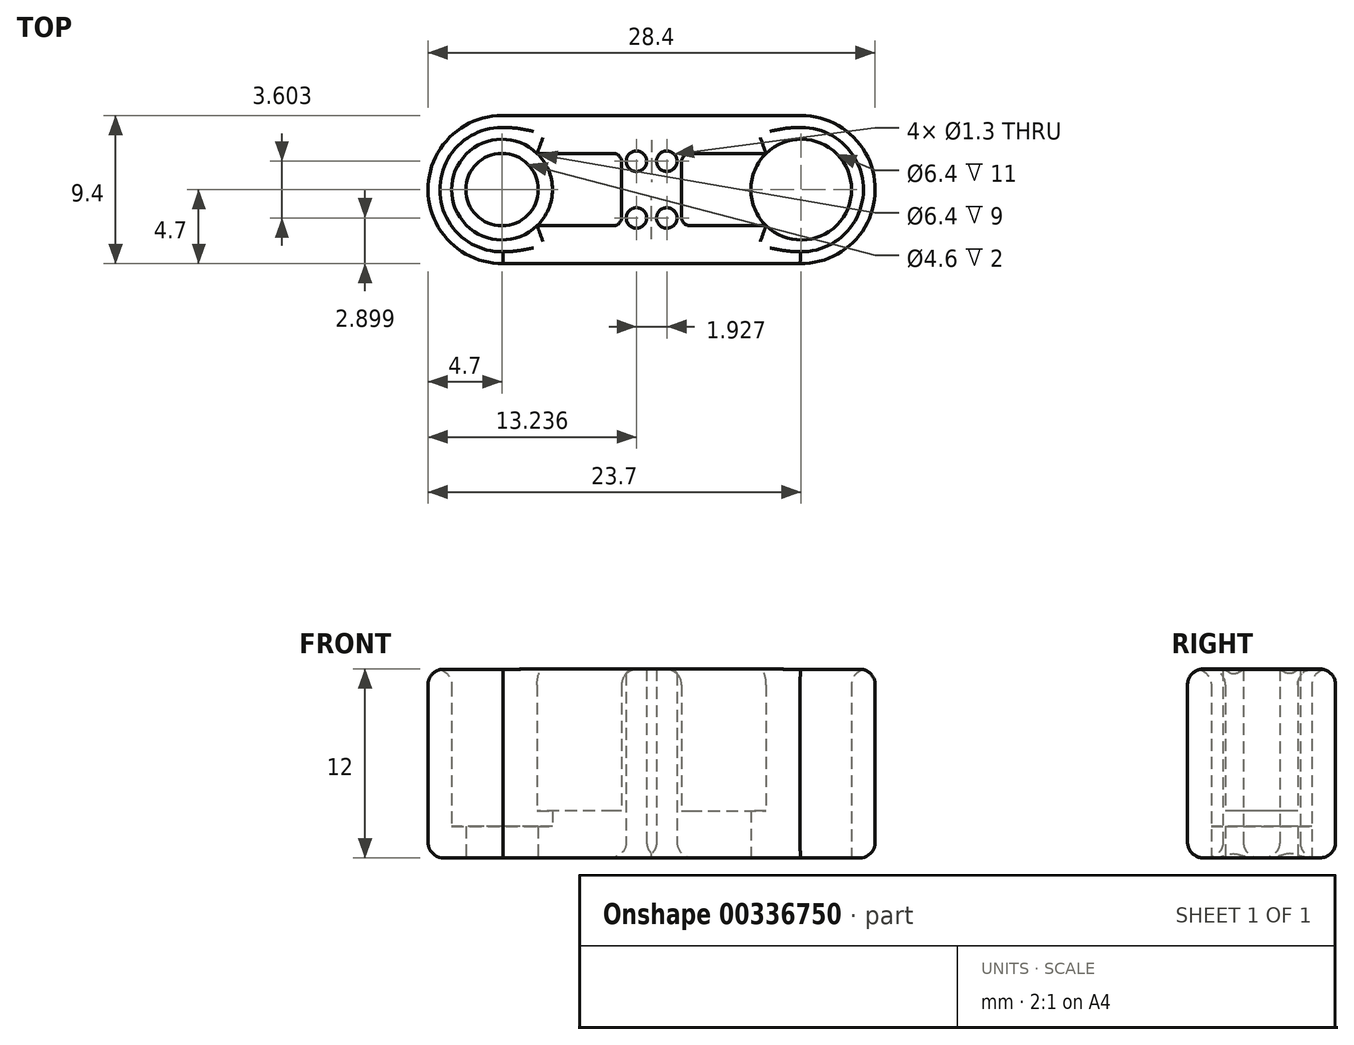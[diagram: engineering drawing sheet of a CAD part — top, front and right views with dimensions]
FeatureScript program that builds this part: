
annotation { "Feature Type Name" : "Feature", "Feature Type Description" : "" }
export const myFeature = defineFeature(function(context is Context, id is Id, definition is map)
    precondition{}
    {
        {
            var Q0;
            Q0=qCreatedBy(makeId("Top.planeOp"),FACE);
            var sketch = newSketch(context, id + "F0", { "sketchPlane" : qUnion([Q0])});
            skCircle(sketch, "E0", {"center": v(-9.5, 0) * mm, "radius": 3.2 * mm});
            skCircle(sketch, "E1", {"center": v(-9.5, 0) * mm, "radius": 2.3 * mm});
            skArc(sketch, "E2.0", {"start": v(-9.5, 4.7) * mm, "mid": v(-14.2, -0.03) * mm, "end": v(-9.44, -4.7) * mm});
            skLineSegment(sketch, "E3", {"start": v(-9.44, -4.7) * mm, "end": v(0, -4.7) * mm});
            skLineSegment(sketch, "E4", {"start": v(-9.5, 4.7) * mm, "end": v(0, 4.7) * mm});
            skLineSegment(sketch, "E5", {"start": v(-1.9, 1.76) * mm, "end": v(-1.9, -1.76) * mm});
            skLineSegment(sketch, "E6", {"start": v(-2.44, 2.3) * mm, "end": v(-9.5, 2.3) * mm});
            skArc(sketch, "E7.filletArc", {"start": v(-1.9, 1.76) * mm, "mid": v(-2.06, 2.14) * mm, "end": v(-2.44, 2.3) * mm});
            skLineSegment(sketch, "E8.MirrorCS", {"start": v(-2.44, -2.3) * mm, "end": v(-9.5, -2.3) * mm});
            skArc(sketch, "E9.MirrorCS", {"start": v(-1.9, -1.76) * mm, "mid": v(-2.06, -2.14) * mm, "end": v(-2.44, -2.3) * mm});
            skCircle(sketch, "E10.MirrorC", {"center": v(9.5, 0) * mm, "radius": 3.2 * mm});
            skCircle(sketch, "E11.MirrorC", {"center": v(9.5, 0) * mm, "radius": 2.3 * mm});
            skArc(sketch, "E12.MirrorCS", {"start": v(9.5, 4.7) * mm, "mid": v(14.2, -0.03) * mm, "end": v(9.44, -4.7) * mm});
            skArc(sketch, "E13.MirrorCS", {"start": v(1.9, -1.76) * mm, "mid": v(2.06, -2.14) * mm, "end": v(2.44, -2.3) * mm});
            skLineSegment(sketch, "E14.MirrorCS", {"start": v(9.44, -4.7) * mm, "end": v(0, -4.7) * mm});
            skLineSegment(sketch, "E15.MirrorCS", {"start": v(2.44, -2.3) * mm, "end": v(9.5, -2.3) * mm});
            skLineSegment(sketch, "E16.MirrorCS", {"start": v(1.9, 1.76) * mm, "end": v(1.9, -1.76) * mm});
            skArc(sketch, "E17.MirrorCS", {"start": v(1.9, 1.76) * mm, "mid": v(2.06, 2.14) * mm, "end": v(2.44, 2.3) * mm});
            skLineSegment(sketch, "E18.MirrorCS", {"start": v(9.5, 4.7) * mm, "end": v(0, 4.7) * mm});
            skLineSegment(sketch, "E19.MirrorCS", {"start": v(2.44, 2.3) * mm, "end": v(9.5, 2.3) * mm});
            skCircle(sketch, "E20", {"center": v(-0.96, 1.8) * mm, "radius": 0.65 * mm});
            skCircle(sketch, "E21.MirrorC", {"center": v(0.96, 1.8) * mm, "radius": 0.65 * mm});
            skCircle(sketch, "E22.MirrorC", {"center": v(0.96, -1.8) * mm, "radius": 0.65 * mm});
            skCircle(sketch, "E23.MirrorC", {"center": v(-0.96, -1.8) * mm, "radius": 0.65 * mm});
            skSolve(sketch);
        }
        {
            var Q0;
            Q0=makeQuery(id+"F0.imprint","IMPRINT",FACE,{"disambiguationData":[TD([[makeQuery(id+"F0.imprint","IMPRINT",EDGE,{"derivedFrom":sQuery(id+"F0.wireOp",EDGE,"E2.0")}),1.0]])]});
            extrude(context, id + "F1", {"entities" : qUnion([Q0]), "depth" : 12 * mm});
        }
        {
            var Q0;
            Q0 = qSketchRegion(id + "F0", true);
            var Q1;
            {var subQ0=sQuery(id+"F0.wireOp",EDGE,"E6");var subQ1=sQuery(id+"F0.wireOp",EDGE,"E0");var subQ2=makeQuery(id+"F0.imprint","INTERSECT",VERTEX,{"derivedFrom":[subQ1,subQ0]});Q1=makeQuery(id+"F0.imprint","IMPRINT",FACE,{"disambiguationData":[TD([[makeQuery(id+"F0.imprint","IMPRINT",EDGE,{"disambiguationData":[TD([[subQ2,1.0]])],"derivedFrom":subQ1}),1.0]])]});}
            var Q2;
            {var subQ0=sQuery(id+"F0.wireOp",EDGE,"E6");var subQ1=sQuery(id+"F0.wireOp",EDGE,"E0");var subQ2=makeQuery(id+"F0.imprint","INTERSECT",VERTEX,{"derivedFrom":[subQ1,subQ0]});Q2=makeQuery(id+"F0.imprint","IMPRINT",FACE,{"disambiguationData":[TD([[makeQuery(id+"F0.imprint","IMPRINT",EDGE,{"disambiguationData":[TD([[subQ2,-1.0]])],"derivedFrom":subQ1}),1.0]])]});}
            var Q3;
            {var subQ0=sQuery(id+"F0.wireOp",EDGE,"E15.MirrorCS");var subQ1=sQuery(id+"F0.wireOp",EDGE,"E10.MirrorC");var subQ2=makeQuery(id+"F0.imprint","INTERSECT",VERTEX,{"derivedFrom":[subQ1,subQ0]});Q3=makeQuery(id+"F0.imprint","IMPRINT",FACE,{"disambiguationData":[TD([[makeQuery(id+"F0.imprint","IMPRINT",EDGE,{"disambiguationData":[TD([[subQ2,-1.0]])],"derivedFrom":subQ1}),-1.0]])]});}
            var Q4;
            {var subQ0=sQuery(id+"F0.wireOp",EDGE,"E15.MirrorCS");var subQ1=sQuery(id+"F0.wireOp",EDGE,"E10.MirrorC");var subQ2=makeQuery(id+"F0.imprint","INTERSECT",VERTEX,{"derivedFrom":[subQ1,subQ0]});Q4=makeQuery(id+"F0.imprint","IMPRINT",FACE,{"disambiguationData":[TD([[makeQuery(id+"F0.imprint","IMPRINT",EDGE,{"disambiguationData":[TD([[subQ2,1.0]])],"derivedFrom":subQ1}),-1.0]])]});}
            extrude(context, id + "F2", {"entities" : qUnion([Q0, Q1, Q2, Q3, Q4]), "operationType" : NewBodyOperationType.ADD, "depth" : 2 * mm});
        }
        {
            var Q0;
            Q0=makeQuery(id+"F0.imprint","IMPRINT",FACE,{"disambiguationData":[TD([[makeQuery(id+"F0.imprint","IMPRINT",EDGE,{"derivedFrom":sQuery(id+"F0.wireOp",EDGE,"E5")}),-1.0]])]});
            var Q1;
            {var subQ1=sQuery(id+"F0.wireOp",EDGE,"E13.MirrorCS");Q1=makeQuery(id+"F0.imprint","IMPRINT",FACE,{"disambiguationData":[TD([[makeQuery(id+"F0.imprint","IMPRINT",EDGE,{"derivedFrom":subQ1}),1.0]])]});}
            extrude(context, id + "F3", {"entities" : qUnion([Q0, Q1]), "operationType" : NewBodyOperationType.ADD, "depth" : 3 * mm});
        }
        {
            var Q0;
            Q0=makeQuery(id+"F1.opExtrude","CAP_EDGE",EDGE,{"disambiguationData":[OSD([sQuery(id+"F0.wireOp",EDGE,"E4"),sQuery(id+"F0.wireOp",EDGE,"E18.MirrorCS")])],"isStart":true});
            var Q1;
            Q1=makeQuery(id+"F1.opExtrude","CAP_EDGE",EDGE,{"disambiguationData":[OSD([sQuery(id+"F0.wireOp",EDGE,"E2.0")])],"isStart":true});
            var Q2;
            Q2=makeQuery(id+"F1.opExtrude","CAP_EDGE",EDGE,{"disambiguationData":[OSD([sQuery(id+"F0.wireOp",EDGE,"E3"),sQuery(id+"F0.wireOp",EDGE,"E14.MirrorCS")])],"isStart":true});
            var Q3;
            Q3=makeQuery(id+"F1.opExtrude","CAP_EDGE",EDGE,{"disambiguationData":[OSD([sQuery(id+"F0.wireOp",EDGE,"E4"),sQuery(id+"F0.wireOp",EDGE,"E18.MirrorCS")])],"isStart":false});
            var Q4;
            Q4=makeQuery(id+"FcPZLXXCWkzdTJN_1.opExtrude","CAP_EDGE",EDGE,{"disambiguationData":[OSD([sQuery(id+"F0.wireOp",EDGE,"da179f35-00f0-428c-ac90-ed6aac98624d0.MirrorCS")])],"isStart":false});
            var Q5;
            Q5=makeQuery(id+"F1.opExtrude","CAP_EDGE",EDGE,{"disambiguationData":[OSD([sQuery(id+"F0.wireOp",EDGE,"E19.MirrorCS")])],"isStart":false});
            var Q6;
            Q6=makeQuery(id+"F1.opExtrude","CAP_EDGE",EDGE,{"disambiguationData":[OSD([sQuery(id+"F0.wireOp",EDGE,"E10.MirrorC")])],"isStart":false});
            var Q7;
            Q7=makeQuery(id+"F1.opExtrude","CAP_EDGE",EDGE,{"disambiguationData":[OSD([sQuery(id+"F0.wireOp",EDGE,"E8.MirrorCS")])],"isStart":false});
            var Q8;
            Q8=makeQuery(id+"F1.opExtrude","CAP_EDGE",EDGE,{"disambiguationData":[OSD([sQuery(id+"F0.wireOp",EDGE,"E9.MirrorCS")])],"isStart":false});
            var Q9;
            Q9=makeQuery(id+"F1.opExtrude","CAP_EDGE",EDGE,{"disambiguationData":[OSD([sQuery(id+"F0.wireOp",EDGE,"E5")])],"isStart":false});
            var Q10;
            Q10=makeQuery(id+"F1.opExtrude","CAP_EDGE",EDGE,{"disambiguationData":[OSD([sQuery(id+"F0.wireOp",EDGE,"E7.filletArc")])],"isStart":false});
            var Q11;
            Q11=makeQuery(id+"F1.opExtrude","CAP_EDGE",EDGE,{"disambiguationData":[OSD([sQuery(id+"F0.wireOp",EDGE,"E6")])],"isStart":false});
            var Q12;
            Q12=makeQuery(id+"F1.opExtrude","CAP_EDGE",EDGE,{"disambiguationData":[OSD([sQuery(id+"F0.wireOp",EDGE,"E0")])],"isStart":false});
            fillet(context, id + "F4", {"entities" : qUnion([Q0, Q1, Q2, Q3, Q4, Q5, Q6, Q7, Q8, Q9, Q10, Q11, Q12]), "radius" : 1 * mm, "tangentPropagation" : true, "allowEdgeOverflow" : false});
        }
        {
            var Q0;
            Q0=makeQuery(id+"F1.opExtrude","CAP_EDGE",EDGE,{"disambiguationData":[OSD([sQuery(id+"F0.wireOp",EDGE,"E23.MirrorC")])],"isStart":true});
            var Q1;
            Q1=makeQuery(id+"F1.opExtrude","CAP_EDGE",EDGE,{"disambiguationData":[OSD([sQuery(id+"F0.wireOp",EDGE,"E22.MirrorC")])],"isStart":true});
            var Q2;
            Q2=makeQuery(id+"F1.opExtrude","CAP_EDGE",EDGE,{"disambiguationData":[OSD([sQuery(id+"F0.wireOp",EDGE,"E21.MirrorC")])],"isStart":true});
            var Q3;
            Q3=makeQuery(id+"F1.opExtrude","CAP_EDGE",EDGE,{"disambiguationData":[OSD([sQuery(id+"F0.wireOp",EDGE,"E20")])],"isStart":true});
            fillet(context, id + "F5", {"entities" : qUnion([Q0, Q1, Q2, Q3]), "radius" : 1 * mm, "tangentPropagation" : true, "allowEdgeOverflow" : false});
        }
    });
